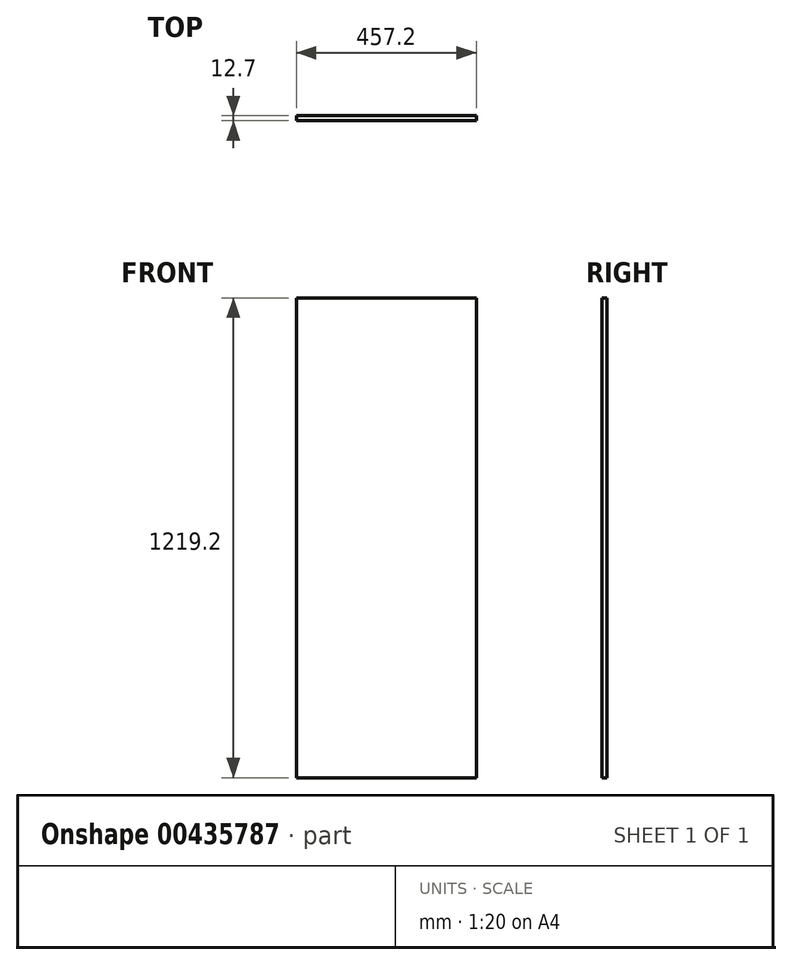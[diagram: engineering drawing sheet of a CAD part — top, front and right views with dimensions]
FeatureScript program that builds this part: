
annotation { "Feature Type Name" : "Feature", "Feature Type Description" : "" }
export const myFeature = defineFeature(function(context is Context, id is Id, definition is map)
    precondition{}
    {
        {
            var Q0;
            Q0=qCreatedBy(makeId("Front.planeOp"),FACE);
            var sketch = newSketch(context, id + "F0", { "sketchPlane" : qUnion([Q0])});
            skLineSegment(sketch, "E0.bottom", {"start": v(228.6, 609.6) * mm, "end": v(-228.6, 609.6) * mm});
            skLineSegment(sketch, "E0.top", {"start": v(228.6, -609.6) * mm, "end": v(-228.6, -609.6) * mm});
            skLineSegment(sketch, "E0.left", {"start": v(228.6, 609.6) * mm, "end": v(228.6, -609.6) * mm});
            skLineSegment(sketch, "E0.right", {"start": v(-228.6, 609.6) * mm, "end": v(-228.6, -609.6) * mm});
            skPoint(sketch, "E0.middle", {"position": v(0, 0) * mm});
            skSolve(sketch);
        }
        {
            var Q0;
            Q0=makeQuery(id+"F0.imprint","IMPRINT",FACE,{"disambiguationData":[TD([[makeQuery(id+"F0.imprint","IMPRINT",EDGE,{"derivedFrom":sQuery(id+"F0.wireOp",EDGE,"E0.bottom")}),1.0]])]});
            extrude(context, id + "F1", {"entities" : qUnion([Q0]), "depth" : 12.7 * mm});
        }
    });
